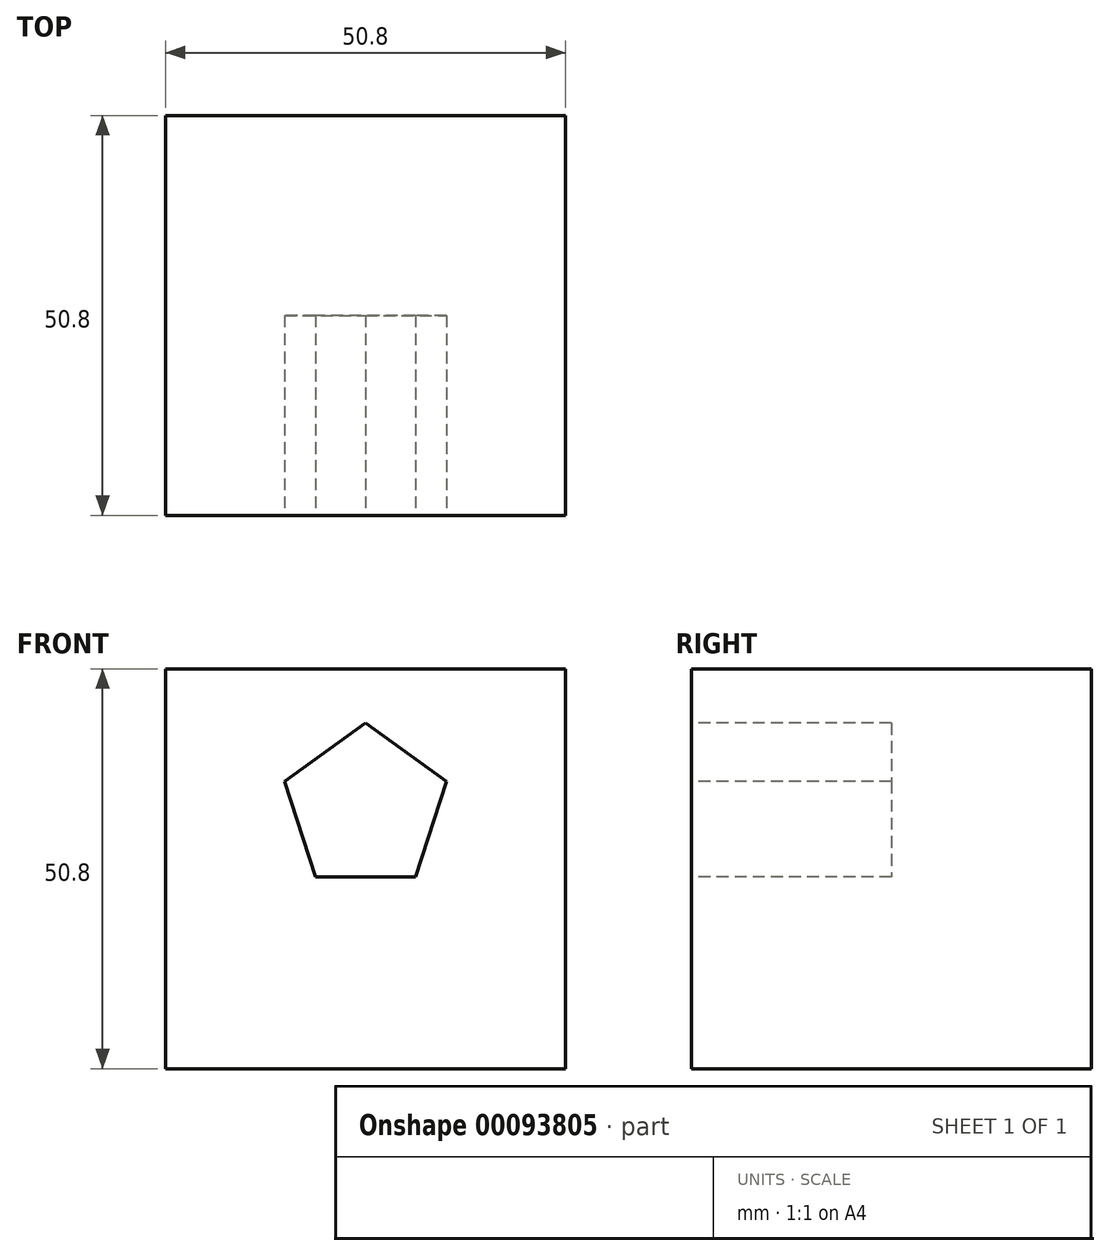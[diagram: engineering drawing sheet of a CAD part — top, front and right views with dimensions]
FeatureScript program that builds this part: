
annotation { "Feature Type Name" : "Feature", "Feature Type Description" : "" }
export const myFeature = defineFeature(function(context is Context, id is Id, definition is map)
    precondition{}
    {
        {
            var Q0;
            Q0=qCreatedBy(makeId("Right.planeOp"),FACE);
            var sketch = newSketch(context, id + "F0", { "sketchPlane" : qUnion([Q0])});
            skLineSegment(sketch, "E0.bottom", {"start": v(-24.95, 26.4) * mm, "end": v(25.85, 26.4) * mm});
            skLineSegment(sketch, "E0.top", {"start": v(-24.95, -24.4) * mm, "end": v(25.85, -24.4) * mm});
            skLineSegment(sketch, "E0.left", {"start": v(-24.95, 26.4) * mm, "end": v(-24.95, -24.4) * mm});
            skLineSegment(sketch, "E0.right", {"start": v(25.85, 26.4) * mm, "end": v(25.85, -24.4) * mm});
            skSolve(sketch);
        }
        {
            var Q0;
            Q0 = qSketchRegion(id + "F0", true);
            extrude(context, id + "F1", {"entities" : qUnion([Q0]), "depth" : 50.8 * mm});
        }
        {
            var Q0;
            Q0=makeQuery(id+"F1.opExtrude","SWEPT_FACE",FACE,{"disambiguationData":[OSD([sQuery(id+"F0.wireOp",EDGE,"E0.left")])]});
            var sketch = newSketch(context, id + "F2", { "sketchPlane" : qUnion([Q0])});
            skCircle(sketch, "E1.cCircle", {"center": v(25.4, 8.74) * mm, "radius": 8.74 * mm, "construction": true});
            skPoint(sketch, "E1.cCircle.centerSnap0", {"position": v(25.4, -24.4) * mm});
            skLineSegment(sketch, "E1.0", {"start": v(31.75, 0) * mm, "end": v(19.05, 0) * mm});
            skLineSegment(sketch, "E1.1", {"start": v(19.05, 0) * mm, "end": v(15.13, 12.07) * mm});
            skLineSegment(sketch, "E1.2", {"start": v(15.13, 12.07) * mm, "end": v(25.4, 19.53) * mm});
            skLineSegment(sketch, "E1.3", {"start": v(25.4, 19.53) * mm, "end": v(35.67, 12.07) * mm});
            skLineSegment(sketch, "E1.4", {"start": v(35.67, 12.07) * mm, "end": v(31.75, 0) * mm});
            skPoint(sketch, "E1.0.midPoint", {"position": v(25.4, 0) * mm});
            skSolve(sketch);
        }
        {
            var Q0;
            Q0 = qSketchRegion(id + "F2", true);
            extrude(context, id + "F3", {"entities" : qUnion([Q0]), "operationType" : NewBodyOperationType.REMOVE, "oppositeDirection" : true, "depth" : 25.4 * mm});
        }
    });
